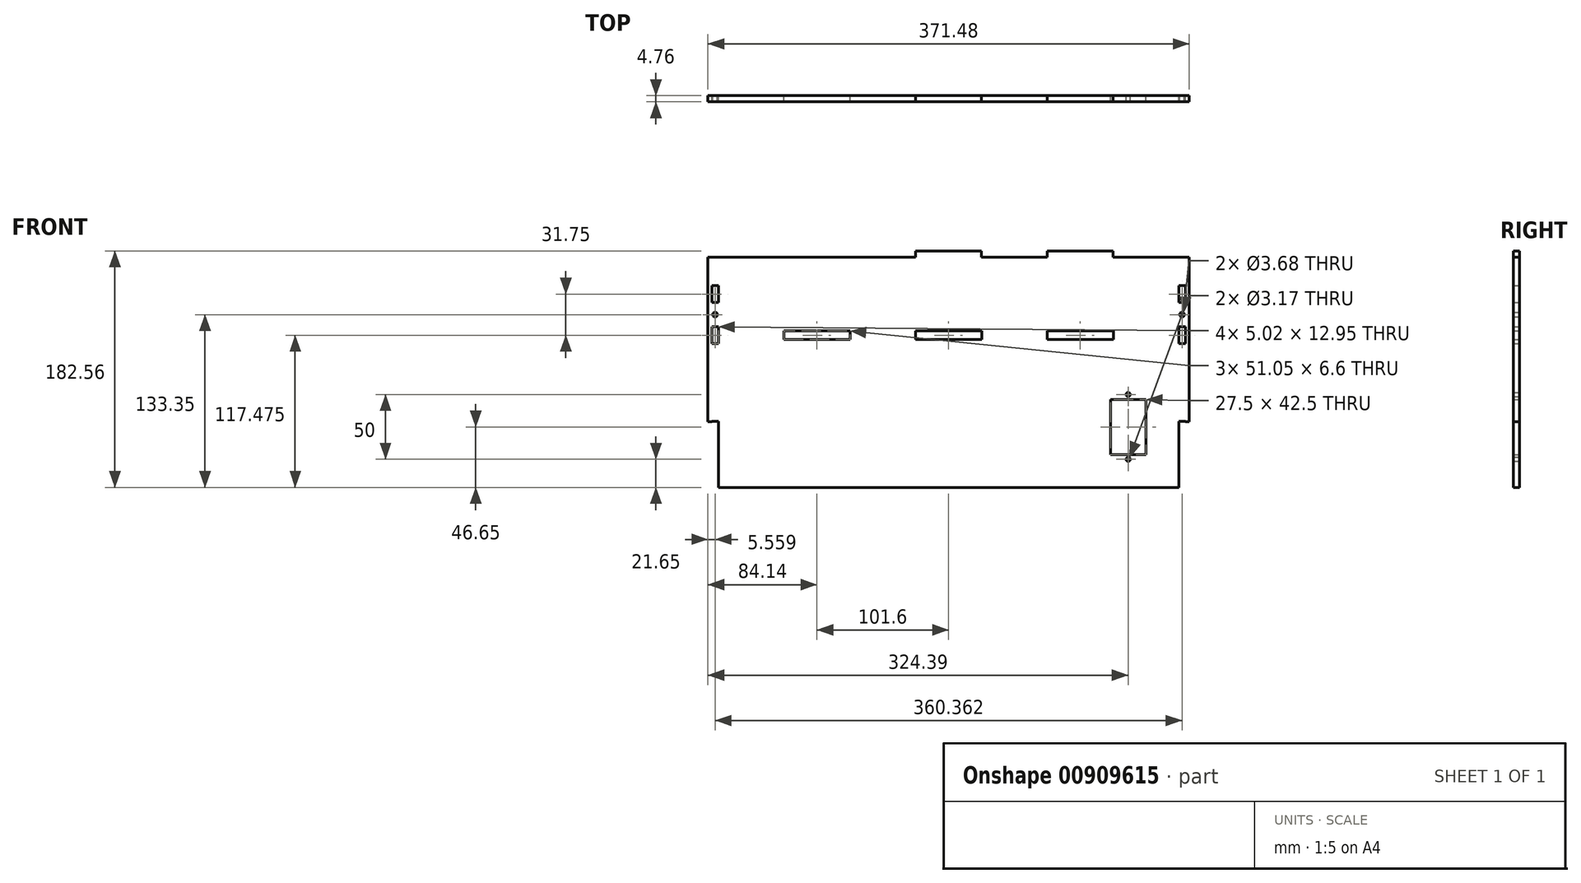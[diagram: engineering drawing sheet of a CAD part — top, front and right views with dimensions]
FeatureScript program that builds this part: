
annotation { "Feature Type Name" : "Feature", "Feature Type Description" : "" }
export const myFeature = defineFeature(function(context is Context, id is Id, definition is map)
    precondition{}
    {
        {
            var Q0;
            Q0=qCreatedBy(makeId("Front.planeOp"),FACE);
            var sketch = newSketch(context, id + "F0", { "sketchPlane" : qUnion([Q0])});
            skLineSegment(sketch, "E0.bottom", {"start": v(-182.56, 88.9) * mm, "end": v(182.56, 88.9) * mm});
            skLineSegment(sketch, "E0.top", {"start": v(-182.56, -88.9) * mm, "end": v(182.56, -88.9) * mm});
            skLineSegment(sketch, "E0.left", {"start": v(-182.56, 88.9) * mm, "end": v(-182.56, -88.9) * mm});
            skLineSegment(sketch, "E0.right", {"start": v(182.56, 88.9) * mm, "end": v(182.56, -88.9) * mm});
            skPoint(sketch, "E0.middle", {"position": v(0, 0) * mm});
            skLineSegment(sketch, "E1.0", {"start": v(-177.8, 88.9) * mm, "end": v(-177.8, -88.9) * mm, "construction": true});
            skLineSegment(sketch, "E2.0", {"start": v(177.8, 88.9) * mm, "end": v(177.8, -88.9) * mm, "construction": true});
            skLineSegment(sketch, "E3.bottom", {"start": v(-127, 31.75) * mm, "end": v(-76.2, 31.75) * mm});
            skLineSegment(sketch, "E3.top", {"start": v(-127, 25.4) * mm, "end": v(-76.2, 25.4) * mm});
            skLineSegment(sketch, "E3.left", {"start": v(-127, 31.75) * mm, "end": v(-127, 25.4) * mm});
            skLineSegment(sketch, "E3.right", {"start": v(-76.2, 31.75) * mm, "end": v(-76.2, 25.4) * mm});
            skLineSegment(sketch, "E4.0", {"start": v(-127.13, 31.88) * mm, "end": v(-76.07, 31.88) * mm});
            skLineSegment(sketch, "E4.1", {"start": v(-127.13, 31.88) * mm, "end": v(-127.13, 25.27) * mm});
            skLineSegment(sketch, "E4.2", {"start": v(-127.13, 25.27) * mm, "end": v(-76.07, 25.27) * mm});
            skLineSegment(sketch, "E4.3", {"start": v(-76.07, 31.88) * mm, "end": v(-76.07, 25.27) * mm});
            skLineSegment(sketch, "E5.1.0.0", {"start": v(-25.53, 31.88) * mm, "end": v(-25.53, 25.27) * mm});
            skLineSegment(sketch, "E5.1.0.1", {"start": v(-25.53, 31.88) * mm, "end": v(25.53, 31.88) * mm});
            skLineSegment(sketch, "E5.1.0.2", {"start": v(-25.53, 25.27) * mm, "end": v(25.53, 25.27) * mm});
            skLineSegment(sketch, "E5.1.0.3", {"start": v(25.4, 31.75) * mm, "end": v(25.4, 25.4) * mm});
            skLineSegment(sketch, "E5.1.0.4", {"start": v(-25.4, 31.75) * mm, "end": v(25.4, 31.75) * mm});
            skLineSegment(sketch, "E5.1.0.5", {"start": v(25.53, 31.88) * mm, "end": v(25.53, 25.27) * mm});
            skLineSegment(sketch, "E5.1.0.6", {"start": v(-25.4, 31.75) * mm, "end": v(-25.4, 25.4) * mm});
            skLineSegment(sketch, "E5.1.0.7", {"start": v(-25.4, 25.4) * mm, "end": v(25.4, 25.4) * mm});
            skLineSegment(sketch, "E5.2.0.0", {"start": v(76.07, 31.88) * mm, "end": v(76.07, 25.27) * mm});
            skLineSegment(sketch, "E5.2.0.1", {"start": v(76.07, 31.88) * mm, "end": v(127.13, 31.88) * mm});
            skLineSegment(sketch, "E5.2.0.2", {"start": v(76.07, 25.27) * mm, "end": v(127.13, 25.27) * mm});
            skLineSegment(sketch, "E5.2.0.3", {"start": v(127, 31.75) * mm, "end": v(127, 25.4) * mm});
            skLineSegment(sketch, "E5.2.0.4", {"start": v(76.2, 31.75) * mm, "end": v(127, 31.75) * mm});
            skLineSegment(sketch, "E5.2.0.5", {"start": v(127.13, 31.88) * mm, "end": v(127.13, 25.27) * mm});
            skLineSegment(sketch, "E5.2.0.6", {"start": v(76.2, 31.75) * mm, "end": v(76.2, 25.4) * mm});
            skLineSegment(sketch, "E5.2.0.7", {"start": v(76.2, 25.4) * mm, "end": v(127, 25.4) * mm});
            skLineSegment(sketch, "E5.direction1", {"start": v(-127, 25.4) * mm, "end": v(-25.4, 25.4) * mm, "construction": true});
            skLineSegment(sketch, "E6.bottom", {"start": v(-182.56, -88.9) * mm, "end": v(-177.8, -88.9) * mm});
            skLineSegment(sketch, "E6.top", {"start": v(-185.74, -38.1) * mm, "end": v(-177.8, -38.1) * mm});
            skLineSegment(sketch, "E6.left", {"start": v(-182.56, -88.9) * mm, "end": v(-182.56, -38.1) * mm});
            skLineSegment(sketch, "E6.right", {"start": v(-177.8, -88.9) * mm, "end": v(-177.8, -38.1) * mm});
            skLineSegment(sketch, "E7", {"start": v(0, 88.9) * mm, "end": v(0, -88.9) * mm, "construction": true});
            skLineSegment(sketch, "E8.MirrorCS", {"start": v(182.56, -88.9) * mm, "end": v(177.8, -88.9) * mm});
            skLineSegment(sketch, "E9.MirrorCS", {"start": v(182.56, -38.1) * mm, "end": v(177.8, -38.1) * mm});
            skLineSegment(sketch, "E10.MirrorCS", {"start": v(182.56, -88.9) * mm, "end": v(182.56, -38.1) * mm});
            skLineSegment(sketch, "E11.MirrorCS", {"start": v(177.8, -88.9) * mm, "end": v(177.8, -38.1) * mm});
            skLineSegment(sketch, "E12.0", {"start": v(-182.69, -89.03) * mm, "end": v(-177.67, -89.03) * mm});
            skLineSegment(sketch, "E12.1", {"start": v(-182.69, -89.03) * mm, "end": v(-182.69, -37.97) * mm});
            skLineSegment(sketch, "E12.2", {"start": v(-182.69, -37.97) * mm, "end": v(-177.67, -37.97) * mm});
            skLineSegment(sketch, "E12.3", {"start": v(-177.67, -89.03) * mm, "end": v(-177.67, -37.97) * mm});
            skLineSegment(sketch, "E13.bottom", {"start": v(-127, 88.9) * mm, "end": v(-76.2, 88.9) * mm});
            skLineSegment(sketch, "E13.top", {"start": v(-127, 93.66) * mm, "end": v(-76.2, 93.66) * mm});
            skLineSegment(sketch, "E13.left", {"start": v(-127, 88.9) * mm, "end": v(-127, 93.66) * mm});
            skLineSegment(sketch, "E13.right", {"start": v(-76.2, 88.9) * mm, "end": v(-76.2, 93.66) * mm});
            skLineSegment(sketch, "E14.1.0.0", {"start": v(-25.4, 93.66) * mm, "end": v(25.4, 93.66) * mm});
            skLineSegment(sketch, "E14.1.0.1", {"start": v(-25.4, 88.9) * mm, "end": v(25.4, 88.9) * mm});
            skLineSegment(sketch, "E14.1.0.2", {"start": v(-25.4, 88.9) * mm, "end": v(-25.4, 93.66) * mm});
            skLineSegment(sketch, "E14.1.0.3", {"start": v(25.4, 88.9) * mm, "end": v(25.4, 93.66) * mm});
            skLineSegment(sketch, "E14.2.0.0", {"start": v(76.2, 93.66) * mm, "end": v(127, 93.66) * mm});
            skLineSegment(sketch, "E14.2.0.1", {"start": v(76.2, 88.9) * mm, "end": v(127, 88.9) * mm});
            skLineSegment(sketch, "E14.2.0.2", {"start": v(76.2, 88.9) * mm, "end": v(76.2, 93.66) * mm});
            skLineSegment(sketch, "E14.2.0.3", {"start": v(127, 88.9) * mm, "end": v(127, 93.66) * mm});
            skLineSegment(sketch, "E14.direction1", {"start": v(-127, 88.9) * mm, "end": v(-25.4, 88.9) * mm, "construction": true});
            skLineSegment(sketch, "E15.MirrorCS", {"start": v(182.69, -89.03) * mm, "end": v(177.67, -89.03) * mm});
            skLineSegment(sketch, "E16.MirrorCS", {"start": v(182.69, -37.97) * mm, "end": v(177.67, -37.97) * mm});
            skLineSegment(sketch, "E17.MirrorCS", {"start": v(182.69, -89.03) * mm, "end": v(182.69, -37.97) * mm});
            skLineSegment(sketch, "E18.MirrorCS", {"start": v(177.67, -89.03) * mm, "end": v(177.67, -37.97) * mm});
            skCircle(sketch, "E19", {"center": v(-180.18, 44.45) * mm, "radius": 1.84 * mm});
            skCircle(sketch, "E20.MirrorC", {"center": v(180.18, 44.45) * mm, "radius": 1.84 * mm});
            skLineSegment(sketch, "E21.0", {"start": v(-185.74, 88.9) * mm, "end": v(-185.74, -38.1) * mm});
            skLineSegment(sketch, "E22", {"start": v(-185.74, 88.9) * mm, "end": v(-182.56, 88.9) * mm});
            skLineSegment(sketch, "E23.MirrorCS", {"start": v(185.74, -38.1) * mm, "end": v(177.8, -38.1) * mm});
            skLineSegment(sketch, "E24.MirrorCS", {"start": v(185.74, 88.9) * mm, "end": v(182.56, 88.9) * mm});
            skLineSegment(sketch, "E25.MirrorCS", {"start": v(185.74, 88.9) * mm, "end": v(185.74, -38.1) * mm});
            skLineSegment(sketch, "E26.bottom", {"start": v(-177.67, 35.05) * mm, "end": v(-182.69, 35.05) * mm});
            skLineSegment(sketch, "E26.top", {"start": v(-177.67, 22.1) * mm, "end": v(-182.69, 22.1) * mm});
            skLineSegment(sketch, "E26.left", {"start": v(-177.67, 35.05) * mm, "end": v(-177.67, 22.1) * mm});
            skLineSegment(sketch, "E26.right", {"start": v(-182.69, 35.05) * mm, "end": v(-182.69, 22.1) * mm});
            skPoint(sketch, "E26.middle", {"position": v(-180.18, 28.58) * mm});
            skPoint(sketch, "E26.middle.positionSnap0", {"position": v(-180.18, -37.97) * mm});
            skPoint(sketch, "E26.centerSnap0", {"position": v(-180.18, -37.97) * mm});
            skLineSegment(sketch, "E27", {"start": v(-185.74, 44.45) * mm, "end": v(-177.8, 44.45) * mm, "construction": true});
            skLineSegment(sketch, "E28.MirrorCS", {"start": v(-177.67, 53.85) * mm, "end": v(-182.69, 53.85) * mm});
            skPoint(sketch, "E29.MirrorP", {"position": v(-180.18, 60.33) * mm});
            skLineSegment(sketch, "E30.MirrorCS", {"start": v(-177.67, 66.8) * mm, "end": v(-182.69, 66.8) * mm});
            skLineSegment(sketch, "E31.MirrorCS", {"start": v(-182.69, 53.85) * mm, "end": v(-182.69, 66.8) * mm});
            skLineSegment(sketch, "E32.MirrorCS", {"start": v(-177.67, 53.85) * mm, "end": v(-177.67, 66.8) * mm});
            skLineSegment(sketch, "E33.MirrorCS", {"start": v(182.69, 53.85) * mm, "end": v(182.69, 66.8) * mm});
            skLineSegment(sketch, "E34.MirrorCS", {"start": v(177.67, 66.8) * mm, "end": v(182.69, 66.8) * mm});
            skLineSegment(sketch, "E35.MirrorCS", {"start": v(177.67, 53.85) * mm, "end": v(177.67, 66.8) * mm});
            skLineSegment(sketch, "E36.MirrorCS", {"start": v(177.67, 53.85) * mm, "end": v(182.69, 53.85) * mm});
            skPoint(sketch, "E37.MirrorP", {"position": v(180.18, 60.33) * mm});
            skLineSegment(sketch, "E38.MirrorCS", {"start": v(177.67, 35.05) * mm, "end": v(182.69, 35.05) * mm});
            skLineSegment(sketch, "E39.MirrorCS", {"start": v(182.69, 35.05) * mm, "end": v(182.69, 22.1) * mm});
            skLineSegment(sketch, "E40.MirrorCS", {"start": v(177.67, 35.05) * mm, "end": v(177.67, 22.1) * mm});
            skLineSegment(sketch, "E41.MirrorCS", {"start": v(177.67, 22.1) * mm, "end": v(182.69, 22.1) * mm});
            skPoint(sketch, "E42.MirrorP", {"position": v(180.18, 28.57) * mm});
            skLineSegment(sketch, "E43.bottom", {"start": v(124.9, -21) * mm, "end": v(152.4, -21) * mm});
            skLineSegment(sketch, "E43.top", {"start": v(124.9, -63.5) * mm, "end": v(152.4, -63.5) * mm});
            skLineSegment(sketch, "E43.left", {"start": v(124.9, -21) * mm, "end": v(124.9, -63.5) * mm});
            skLineSegment(sketch, "E43.right", {"start": v(152.4, -21) * mm, "end": v(152.4, -63.5) * mm});
            skCircle(sketch, "E44", {"center": v(138.65, -17.25) * mm, "radius": 1.59 * mm});
            skPoint(sketch, "E44.centerSnap0", {"position": v(138.65, -21) * mm});
            skLineSegment(sketch, "E45", {"start": v(124.9, -42.25) * mm, "end": v(152.4, -42.25) * mm, "construction": true});
            skCircle(sketch, "E46.MirrorC", {"center": v(138.65, -67.25) * mm, "radius": 1.59 * mm});
            skSolve(sketch);
        }
        {
            var Q0;
            Q0=makeQuery(id+"F0.imprint","IMPRINT",FACE,{"disambiguationData":[TD([[makeQuery(id+"F0.imprint","IMPRINT",EDGE,{"derivedFrom":sQuery(id+"F0.wireOp",EDGE,"E0.bottom")}),-1.0]])]});
            var Q1;
            Q1=makeQuery(id+"F0.imprint","IMPRINT",FACE,{"disambiguationData":[TD([[makeQuery(id+"F0.imprint","IMPRINT",EDGE,{"derivedFrom":sQuery(id+"F0.wireOp",EDGE,"E13.bottom")}),1.0]])]});
            var Q2;
            Q2=makeQuery(id+"F0.imprint","IMPRINT",FACE,{"disambiguationData":[TD([[makeQuery(id+"F0.imprint","IMPRINT",EDGE,{"derivedFrom":sQuery(id+"F0.wireOp",EDGE,"E14.1.0.0")}),-1.0]])]});
            var Q3;
            Q3=makeQuery(id+"F0.imprint","IMPRINT",FACE,{"disambiguationData":[TD([[makeQuery(id+"F0.imprint","IMPRINT",EDGE,{"derivedFrom":sQuery(id+"F0.wireOp",EDGE,"E14.2.0.0")}),-1.0]])]});
            var Q4;
            {var subQ9=sQuery(id+"F0.wireOp",EDGE,"E22");Q4=makeQuery(id+"F0.imprint","IMPRINT",FACE,{"disambiguationData":[TD([[makeQuery(id+"F0.imprint","IMPRINT",EDGE,{"derivedFrom":subQ9}),-1.0]])]});}
            var Q5;
            {var subQ6=sQuery(id+"F0.wireOp",EDGE,"E24.MirrorCS");Q5=makeQuery(id+"F0.imprint","IMPRINT",FACE,{"disambiguationData":[TD([[makeQuery(id+"F0.imprint","IMPRINT",EDGE,{"derivedFrom":subQ6}),1.0]])]});}
            extrude(context, id + "F1", {"entities" : qUnion([Q0, Q1, Q2, Q3, Q4, Q5]), "depth" : 4.76 * mm, "offsetDistance" : 25.4 * mm});
        }
    });
